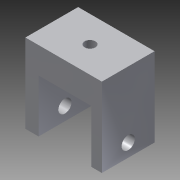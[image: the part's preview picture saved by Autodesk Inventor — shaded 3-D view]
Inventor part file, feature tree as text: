
AUTODESK INVENTOR PART (.ipt)
format: ipt  version: 2013 (Build 170138000, 138)  size: 101,376 bytes
history: native  units: in
note: dims shown in document units (in); Inventor stores cm internally (conversion verified against a paired STEP export)
features: extrude x3, sketch x3
ambient origin geometry x8: Origin, YZ Plane, XZ Plane, XY Plane, X Axis, Y Axis, Z Axis, Center Point
bodies: Solid1 (feature_tree)
feature tree (6):
  extrude  "Extrusion1"  Depth=0.5in
  extrude  "Extrusion2"  Depth=0.75in
  extrude  "Extrusion3"  Depth=0.5in TaperAngle=0.0deg
  sketch  "Sketch1"  dims[d0=0.5in d1=0.5in]
  sketch  "Sketch2"  dims[d2=0.125in d4=0.75in]
  sketch  "Sketch3"  dims[d5=0.725in d6=0.5in d7=0.0in d8=0.1015in d10=1.0in d11=0.0in d12=0.125in d14=0.125in d15=1.0in d16=0.0in]
